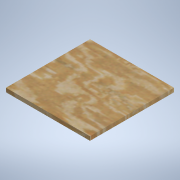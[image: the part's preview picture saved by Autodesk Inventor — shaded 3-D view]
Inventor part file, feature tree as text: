
AUTODESK INVENTOR PART (.ipt)
format: ipt  version: 2021.1 (Build 251245000, 245)  size: 115,200 bytes
history: native  units: mm
features: other x3, extrude x1, sketch x1, reference x1
ambient origin geometry x8: Origin, YZ Plane, XZ Plane, XY Plane, X Axis, Y Axis, Z Axis, Center Point
bodies: Solid1 (feature_tree)
feature tree (6):
  extrude  "Extrusion1"  [1 undecoded]
  sketch  "Sketch1"  dims[d2=270.0mm d3=0.0mm]
  reference  "Reference1"
  other  "<userpath>\Documents\Kerbal Kontroller\Design\Final\Inventor\Final.iam"
  other  "Final.iam"
  other  "Sides:1"
note: 1 required parameter value undecoded (feature->parameter linkage not recoverable at this tier; creation-order binding heuristic only, values carry confidence <= 0.55)
